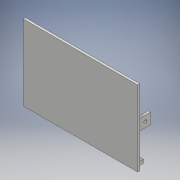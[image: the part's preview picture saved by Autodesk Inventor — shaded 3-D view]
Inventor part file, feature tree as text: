
AUTODESK INVENTOR PART (.ipt)
format: ipt  version: 2018 (Build 220112000, 112)  size: 216,064 bytes
history: native  units: mm
features: extrude x9, sketch x9, other x2
ambient origin geometry x8: Origin, YZ Plane, XZ Plane, XY Plane, X Axis, Y Axis, Z Axis, Center Point
bodies: Body1 (feature_tree)
feature tree (20):
  extrude  "Extrusão4"  Depth=103.0mm
  extrude  "Extrusão5"  Depth=3.1mm
  extrude  "Extrusão6"  Depth=3.1mm
  extrude  "Extrusão7"  Depth=3.0mm
  extrude  "Extrusão8"  Depth=3.0mm
  other  "Plano de trabalho1"
  other  "Plano de trabalho2"
  extrude  "Extrusão9"  Depth=3.0mm TaperAngle=0.0deg
  extrude  "Extrusão10"  Depth=5.0mm
  extrude  "Extrusão13"  Depth=8.0mm
  extrude  "Extrusão14"  Depth=5.0mm TaperAngle=0.0deg
  sketch  "Esboço6"  dims[d22=156.0mm d23=103.0mm]
  sketch  "Esboço7"  dims[d24=3.0mm d25=0.0mm d26=3.1mm]
  sketch  "Esboço10"  dims[d27=3.1mm d28=3.1mm]
  sketch  "Esboço13"  dims[d29=3.1mm d30=3.0mm]
  sketch  "Esboço14"  dims[d31=3.0mm d32=3.0mm]
  sketch  "Esboço18"  dims[d33=3.0mm d34=3.0mm d35=0.0mm]
  sketch  "Esboço19"  dims[d36=5.0mm d37=5.0mm]
  sketch  "Esboço21"  dims[d38=85.0mm d39=8.0mm]
  sketch  "Esboço22"  dims[d40=5.0mm d41=5.0mm d42=0.0mm d43=6.0mm d44=0.0mm d45=8.0mm d46=20.0mm d47=3.0mm d48=5.0mm d49=0.0mm d51=2.0mm d52=0.0mm d53=8.0mm d54=5.0mm d55=5.0mm d65=3.0mm d66=0.0mm d67=15.0mm d68=15.0mm d71=40.9mm d72=15.0mm d73=15.0mm d74=40.9mm d75=3.0mm d76=0.0mm d87=7.5mm d88=7.5mm d89=4.1mm d90=3.0mm d91=0.0mm d92=2.0mm d93=7.0mm d94=10.0mm d95=0.0mm]
